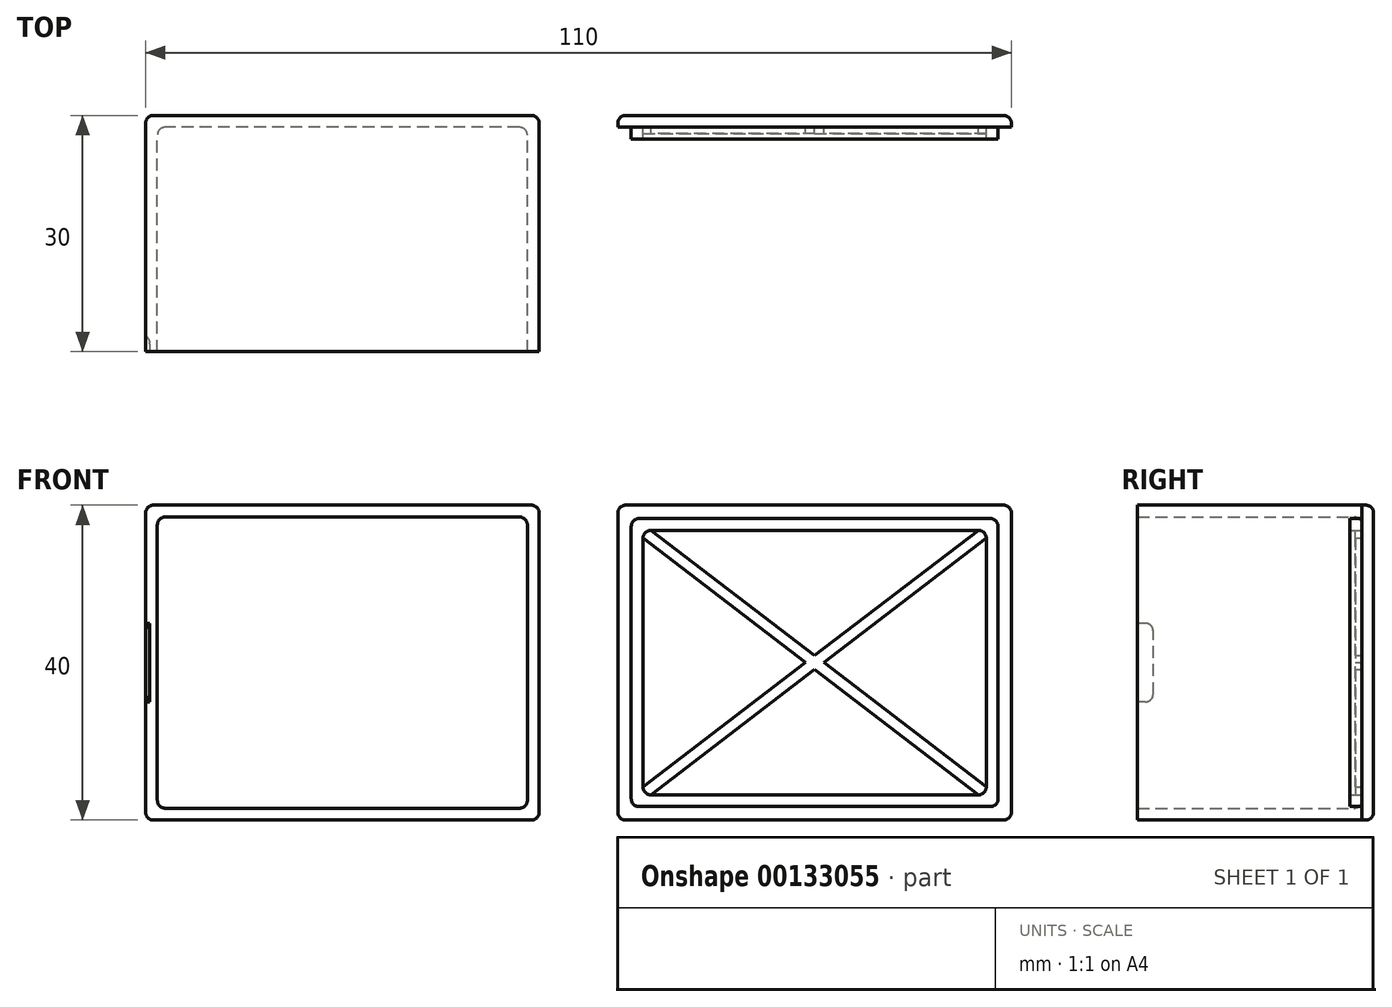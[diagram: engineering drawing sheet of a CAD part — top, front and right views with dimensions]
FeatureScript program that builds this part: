
annotation { "Feature Type Name" : "Feature", "Feature Type Description" : "" }
export const myFeature = defineFeature(function(context is Context, id is Id, definition is map)
    precondition{}
    {
        {
            var Q0;
            Q0=qCreatedBy(makeId("Front.planeOp"),FACE);
            var sketch = newSketch(context, id + "F0", { "sketchPlane" : qUnion([Q0])});
            skLineSegment(sketch, "E0.bottom", {"start": v(0, 0) * mm, "end": v(50, 0) * mm});
            skLineSegment(sketch, "E0.top", {"start": v(0, 40) * mm, "end": v(50, 40) * mm});
            skLineSegment(sketch, "E0.left", {"start": v(0, 0) * mm, "end": v(0, 40) * mm});
            skLineSegment(sketch, "E0.right", {"start": v(50, 0) * mm, "end": v(50, 40) * mm});
            skLineSegment(sketch, "E1.bottom", {"start": v(1.5, 38.5) * mm, "end": v(48.5, 38.5) * mm});
            skLineSegment(sketch, "E1.top", {"start": v(1.5, 1.5) * mm, "end": v(48.5, 1.5) * mm});
            skLineSegment(sketch, "E1.left", {"start": v(1.5, 38.5) * mm, "end": v(1.5, 1.5) * mm});
            skLineSegment(sketch, "E1.right", {"start": v(48.5, 38.5) * mm, "end": v(48.5, 1.5) * mm});
            skLineSegment(sketch, "E2", {"start": v(25, 0) * mm, "end": v(25, 40) * mm, "construction": true});
            skLineSegment(sketch, "E3", {"start": v(0, 20) * mm, "end": v(50, 20) * mm, "construction": true});
            skLineSegment(sketch, "E4", {"start": v(60, 20) * mm, "end": v(110, 20) * mm, "construction": true});
            skLineSegment(sketch, "E5", {"start": v(85, 0) * mm, "end": v(85, 40) * mm, "construction": true});
            skLineSegment(sketch, "E6.bottom", {"start": v(60, 40) * mm, "end": v(110, 40) * mm});
            skLineSegment(sketch, "E6.top", {"start": v(60, 0) * mm, "end": v(110, 0) * mm});
            skLineSegment(sketch, "E6.left", {"start": v(60, 40) * mm, "end": v(60, 0) * mm});
            skLineSegment(sketch, "E6.right", {"start": v(110, 40) * mm, "end": v(110, 0) * mm});
            skLineSegment(sketch, "E7.bottom", {"start": v(61.5, 38.5) * mm, "end": v(108.5, 38.5) * mm, "construction": true});
            skLineSegment(sketch, "E7.top", {"start": v(61.5, 1.5) * mm, "end": v(108.5, 1.5) * mm, "construction": true});
            skLineSegment(sketch, "E7.left", {"start": v(61.5, 38.5) * mm, "end": v(61.5, 1.5) * mm, "construction": true});
            skLineSegment(sketch, "E7.right", {"start": v(108.5, 38.5) * mm, "end": v(108.5, 1.5) * mm, "construction": true});
            skLineSegment(sketch, "E8.bottom", {"start": v(61.7, 38.3) * mm, "end": v(108.3, 38.3) * mm});
            skLineSegment(sketch, "E8.top", {"start": v(61.7, 1.7) * mm, "end": v(108.3, 1.7) * mm});
            skLineSegment(sketch, "E8.left", {"start": v(61.7, 38.3) * mm, "end": v(61.7, 1.7) * mm});
            skLineSegment(sketch, "E8.right", {"start": v(108.3, 38.3) * mm, "end": v(108.3, 1.7) * mm});
            skLineSegment(sketch, "E9", {"start": v(1.5, 38.5) * mm, "end": v(0, 38.5) * mm, "construction": true});
            skLineSegment(sketch, "E10", {"start": v(1.5, 38.5) * mm, "end": v(1.5, 40) * mm, "construction": true});
            skText(sketch, "E11", { "text": "Длина\nШирина\nТолщина стенок\nЗазор в ответной части", "fontName": "OpenSans-Regular.ttf"});
            skLineSegment(sketch, "E12", {"start": v(12.68, 60) * mm, "end": v(49.68, 60) * mm, "construction": true});
            skLineSegment(sketch, "E13", {"start": v(12.68, 57.5) * mm, "end": v(59.68, 57.5) * mm, "construction": true});
            skLineSegment(sketch, "E14", {"start": v(12.68, 55) * mm, "end": v(14.18, 55) * mm, "construction": true});
            skLineSegment(sketch, "E15", {"start": v(12.68, 52.5) * mm, "end": v(12.88, 52.5) * mm, "construction": true});
            skLineSegment(sketch, "E16", {"start": v(61.5, 38.5) * mm, "end": v(61.5, 40) * mm, "construction": true});
            skLineSegment(sketch, "E17", {"start": v(61.5, 38.5) * mm, "end": v(60, 38.5) * mm, "construction": true});
            skLineSegment(sketch, "E18", {"start": v(61.7, 38.3) * mm, "end": v(61.7, 38.5) * mm, "construction": true});
            skLineSegment(sketch, "E19", {"start": v(61.7, 38.3) * mm, "end": v(61.5, 38.3) * mm, "construction": true});
            skLineSegment(sketch, "E20.bottom", {"start": v(63.2, 36.8) * mm, "end": v(106.8, 36.8) * mm});
            skLineSegment(sketch, "E20.top", {"start": v(63.2, 3.2) * mm, "end": v(106.8, 3.2) * mm});
            skLineSegment(sketch, "E20.left", {"start": v(63.2, 36.8) * mm, "end": v(63.2, 3.2) * mm});
            skLineSegment(sketch, "E20.right", {"start": v(106.8, 36.8) * mm, "end": v(106.8, 3.2) * mm});
            skLineSegment(sketch, "E21", {"start": v(63.2, 36.8) * mm, "end": v(63.2, 38.3) * mm, "construction": true});
            skLineSegment(sketch, "E22", {"start": v(63.2, 36.8) * mm, "end": v(61.7, 36.8) * mm, "construction": true});
            const initialGuessF0  = {"E11": [-0.0124, 0.05874, 1, 0, 0.00126]};
            skSetInitialGuess(sketch, initialGuessF0);
            skSolve(sketch);
        }
        {
            var Q0;
            Q0=makeQuery(id+"F0.imprint","IMPRINT",FACE,{"disambiguationData":[TD([[makeQuery(id+"F0.imprint","IMPRINT",EDGE,{"derivedFrom":sQuery(id+"F0.wireOp",EDGE,"E1.bottom")}),-1.0]])]});
            var Q1;
            Q1=makeQuery(id+"F0.imprint","IMPRINT",FACE,{"disambiguationData":[TD([[makeQuery(id+"F0.imprint","IMPRINT",EDGE,{"derivedFrom":sQuery(id+"F0.wireOp",EDGE,"E0.bottom")}),1.0]])]});
            var Q2;
            Q2=makeQuery(id+"F0.imprint","IMPRINT",FACE,{"disambiguationData":[TD([[makeQuery(id+"F0.imprint","IMPRINT",EDGE,{"derivedFrom":sQuery(id+"F0.wireOp",EDGE,"E6.bottom")}),-1.0]])]});
            var Q3;
            Q3=makeQuery(id+"F0.imprint","IMPRINT",FACE,{"disambiguationData":[TD([[makeQuery(id+"F0.imprint","IMPRINT",EDGE,{"derivedFrom":sQuery(id+"F0.wireOp",EDGE,"E7.bottom")}),-1.0]])]});
            var Q4;
            Q4=makeQuery(id+"F0.imprint","IMPRINT",FACE,{"disambiguationData":[TD([[makeQuery(id+"F0.imprint","IMPRINT",EDGE,{"derivedFrom":sQuery(id+"F0.wireOp",EDGE,"E8.bottom")}),-1.0]])]});
            var Q5;
            Q5=makeQuery(id+"F0.imprint","IMPRINT",FACE,{"disambiguationData":[TD([[makeQuery(id+"F0.imprint","IMPRINT",EDGE,{"derivedFrom":sQuery(id+"F0.wireOp",EDGE,"E20.bottom")}),-1.0]])]});
            extrude(context, id + "F1", {"entities" : qUnion([Q0, Q1, Q2, Q3, Q4, Q5]), "depth" : 1.5 * mm, "offsetDistance" : 25 * mm});
        }
        {
            var Q0;
            Q0=makeQuery(id+"F0.imprint","IMPRINT",FACE,{"disambiguationData":[TD([[makeQuery(id+"F0.imprint","IMPRINT",EDGE,{"derivedFrom":sQuery(id+"F0.wireOp",EDGE,"E0.bottom")}),1.0]])]});
            extrude(context, id + "F2", {"entities" : qUnion([Q0]), "operationType" : NewBodyOperationType.ADD, "depth" : 30 * mm, "offsetDistance" : 25 * mm});
        }
        {
            var Q0;
            Q0=makeQuery(id+"F0.imprint","IMPRINT",FACE,{"disambiguationData":[TD([[makeQuery(id+"F0.imprint","IMPRINT",EDGE,{"derivedFrom":sQuery(id+"F0.wireOp",EDGE,"E8.bottom")}),-1.0]])]});
            extrude(context, id + "F3", {"entities" : qUnion([Q0]), "operationType" : NewBodyOperationType.ADD, "depth" : (1 + 2) * mm});
        }
        {
            var Q0;
            {var subQ0=sQuery(id+"F0.wireOp",EDGE,"E0.right");var subQ1=sQuery(id+"F0.wireOp",EDGE,"E0.bottom");Q0=makeQuery(id+"F2.boolean.opBoolean","MERGE",EDGE,{"derivedFrom":[makeQuery(id+"F1.opExtrude","SWEPT_EDGE",EDGE,{"disambiguationData":[OSD([subQ1,subQ0])]}),makeQuery(id+"F2.opExtrude","SWEPT_EDGE",EDGE,{"disambiguationData":[OSD([subQ1,subQ0])]})]});}
            var Q1;
            {var subQ0=sQuery(id+"F0.wireOp",EDGE,"E0.left");var subQ1=sQuery(id+"F0.wireOp",EDGE,"E0.bottom");Q1=makeQuery(id+"F2.boolean.opBoolean","MERGE",EDGE,{"derivedFrom":[makeQuery(id+"F1.opExtrude","SWEPT_EDGE",EDGE,{"disambiguationData":[OSD([subQ1,subQ0])]}),makeQuery(id+"F2.opExtrude","SWEPT_EDGE",EDGE,{"disambiguationData":[OSD([subQ1,subQ0])]})]});}
            var Q2;
            {var subQ0=sQuery(id+"F0.wireOp",EDGE,"E0.left");var subQ1=sQuery(id+"F0.wireOp",EDGE,"E0.top");Q2=makeQuery(id+"F2.boolean.opBoolean","MERGE",EDGE,{"derivedFrom":[makeQuery(id+"F1.opExtrude","SWEPT_EDGE",EDGE,{"disambiguationData":[OSD([subQ1,subQ0])]}),makeQuery(id+"F2.opExtrude","SWEPT_EDGE",EDGE,{"disambiguationData":[OSD([subQ1,subQ0])]})]});}
            var Q3;
            {var subQ0=sQuery(id+"F0.wireOp",EDGE,"E0.right");var subQ1=sQuery(id+"F0.wireOp",EDGE,"E0.top");Q3=makeQuery(id+"F2.boolean.opBoolean","MERGE",EDGE,{"derivedFrom":[makeQuery(id+"F1.opExtrude","SWEPT_EDGE",EDGE,{"disambiguationData":[OSD([subQ1,subQ0])]}),makeQuery(id+"F2.opExtrude","SWEPT_EDGE",EDGE,{"disambiguationData":[OSD([subQ1,subQ0])]})]});}
            var Q4;
            Q4=makeQuery(id+"F1.opExtrude","CAP_EDGE",EDGE,{"disambiguationData":[OSD([sQuery(id+"F0.wireOp",EDGE,"E0.top")])],"isStart":true});
            var Q5;
            Q5=makeQuery(id+"F1.opExtrude","CAP_EDGE",EDGE,{"disambiguationData":[OSD([sQuery(id+"F0.wireOp",EDGE,"E0.left")])],"isStart":true});
            var Q6;
            Q6=makeQuery(id+"F1.opExtrude","CAP_EDGE",EDGE,{"disambiguationData":[OSD([sQuery(id+"F0.wireOp",EDGE,"E0.bottom")])],"isStart":true});
            var Q7;
            Q7=makeQuery(id+"F1.opExtrude","CAP_EDGE",EDGE,{"disambiguationData":[OSD([sQuery(id+"F0.wireOp",EDGE,"E0.right")])],"isStart":true});
            var Q8;
            Q8=makeQuery(id+"F1.opExtrude","CAP_EDGE",EDGE,{"disambiguationData":[OSD([sQuery(id+"F0.wireOp",EDGE,"E6.bottom")])],"isStart":true});
            var Q9;
            Q9=makeQuery(id+"F1.opExtrude","CAP_EDGE",EDGE,{"disambiguationData":[OSD([sQuery(id+"F0.wireOp",EDGE,"E6.left")])],"isStart":true});
            var Q10;
            Q10=makeQuery(id+"F1.opExtrude","CAP_EDGE",EDGE,{"disambiguationData":[OSD([sQuery(id+"F0.wireOp",EDGE,"E6.top")])],"isStart":true});
            var Q11;
            Q11=makeQuery(id+"F1.opExtrude","CAP_EDGE",EDGE,{"disambiguationData":[OSD([sQuery(id+"F0.wireOp",EDGE,"E6.right")])],"isStart":true});
            var Q12;
            Q12=makeQuery(id+"F1.opExtrude","SWEPT_EDGE",EDGE,{"disambiguationData":[OSD([sQuery(id+"F0.wireOp",EDGE,"E6.top"),sQuery(id+"F0.wireOp",EDGE,"E6.left")])]});
            var Q13;
            Q13=makeQuery(id+"F1.opExtrude","SWEPT_EDGE",EDGE,{"disambiguationData":[OSD([sQuery(id+"F0.wireOp",EDGE,"E6.bottom"),sQuery(id+"F0.wireOp",EDGE,"E6.left")])]});
            var Q14;
            Q14=makeQuery(id+"F1.opExtrude","SWEPT_EDGE",EDGE,{"disambiguationData":[OSD([sQuery(id+"F0.wireOp",EDGE,"E6.bottom"),sQuery(id+"F0.wireOp",EDGE,"E6.right")])]});
            var Q15;
            Q15=makeQuery(id+"F1.opExtrude","SWEPT_EDGE",EDGE,{"disambiguationData":[OSD([sQuery(id+"F0.wireOp",EDGE,"E6.top"),sQuery(id+"F0.wireOp",EDGE,"E6.right")])]});
            var Q16;
            Q16=makeQuery(id+"F2.opExtrude","SWEPT_EDGE",EDGE,{"disambiguationData":[OSD([sQuery(id+"F0.wireOp",EDGE,"E1.bottom"),sQuery(id+"F0.wireOp",EDGE,"E1.right")])]});
            var Q17;
            Q17=makeQuery(id+"F2.opExtrude","SWEPT_EDGE",EDGE,{"disambiguationData":[OSD([sQuery(id+"F0.wireOp",EDGE,"E1.top"),sQuery(id+"F0.wireOp",EDGE,"E1.right")])]});
            var Q18;
            Q18=makeQuery(id+"F2.opExtrude","SWEPT_EDGE",EDGE,{"disambiguationData":[OSD([sQuery(id+"F0.wireOp",EDGE,"E1.bottom"),sQuery(id+"F0.wireOp",EDGE,"E1.left")])]});
            var Q19;
            Q19=makeQuery(id+"F2.opExtrude","SWEPT_EDGE",EDGE,{"disambiguationData":[OSD([sQuery(id+"F0.wireOp",EDGE,"E1.top"),sQuery(id+"F0.wireOp",EDGE,"E1.left")])]});
            var Q20;
            Q20=makeQuery(id+"F2.boolean.opBoolean","INTERSECT",EDGE,{"derivedFrom":[makeQuery(id+"F1.opExtrude","CAP_FACE",FACE,{"disambiguationData":[OSD([sQuery(id+"F0.wireOp",EDGE,"E0.bottom"),sQuery(id+"F0.wireOp",EDGE,"E0.top"),sQuery(id+"F0.wireOp",EDGE,"E0.left"),sQuery(id+"F0.wireOp",EDGE,"E0.right")])],"isStart":false}),makeQuery(id+"F2.opExtrude","SWEPT_FACE",FACE,{"disambiguationData":[OSD([sQuery(id+"F0.wireOp",EDGE,"E1.left")])]})]});
            var Q21;
            Q21=makeQuery(id+"F2.boolean.opBoolean","INTERSECT",EDGE,{"derivedFrom":[makeQuery(id+"F1.opExtrude","CAP_FACE",FACE,{"disambiguationData":[OSD([sQuery(id+"F0.wireOp",EDGE,"E0.bottom"),sQuery(id+"F0.wireOp",EDGE,"E0.top"),sQuery(id+"F0.wireOp",EDGE,"E0.left"),sQuery(id+"F0.wireOp",EDGE,"E0.right")])],"isStart":false}),makeQuery(id+"F2.opExtrude","SWEPT_FACE",FACE,{"disambiguationData":[OSD([sQuery(id+"F0.wireOp",EDGE,"E1.bottom")])]})]});
            var Q22;
            Q22=makeQuery(id+"F2.boolean.opBoolean","INTERSECT",EDGE,{"derivedFrom":[makeQuery(id+"F1.opExtrude","CAP_FACE",FACE,{"disambiguationData":[OSD([sQuery(id+"F0.wireOp",EDGE,"E0.bottom"),sQuery(id+"F0.wireOp",EDGE,"E0.top"),sQuery(id+"F0.wireOp",EDGE,"E0.left"),sQuery(id+"F0.wireOp",EDGE,"E0.right")])],"isStart":false}),makeQuery(id+"F2.opExtrude","SWEPT_FACE",FACE,{"disambiguationData":[OSD([sQuery(id+"F0.wireOp",EDGE,"E1.right")])]})]});
            var Q23;
            Q23=makeQuery(id+"F2.boolean.opBoolean","INTERSECT",EDGE,{"derivedFrom":[makeQuery(id+"F1.opExtrude","CAP_FACE",FACE,{"disambiguationData":[OSD([sQuery(id+"F0.wireOp",EDGE,"E0.bottom"),sQuery(id+"F0.wireOp",EDGE,"E0.top"),sQuery(id+"F0.wireOp",EDGE,"E0.left"),sQuery(id+"F0.wireOp",EDGE,"E0.right")])],"isStart":false}),makeQuery(id+"F2.opExtrude","SWEPT_FACE",FACE,{"disambiguationData":[OSD([sQuery(id+"F0.wireOp",EDGE,"E1.top")])]})]});
            var Q24;
            Q24=makeQuery(id+"F3.opExtrude","SWEPT_EDGE",EDGE,{"disambiguationData":[OSD([sQuery(id+"F0.wireOp",EDGE,"E8.top"),sQuery(id+"F0.wireOp",EDGE,"E8.left")])]});
            var Q25;
            Q25=makeQuery(id+"F3.opExtrude","SWEPT_EDGE",EDGE,{"disambiguationData":[OSD([sQuery(id+"F0.wireOp",EDGE,"E8.top"),sQuery(id+"F0.wireOp",EDGE,"E8.right")])]});
            var Q26;
            Q26=makeQuery(id+"F3.opExtrude","SWEPT_EDGE",EDGE,{"disambiguationData":[OSD([sQuery(id+"F0.wireOp",EDGE,"E8.bottom"),sQuery(id+"F0.wireOp",EDGE,"E8.right")])]});
            var Q27;
            Q27=makeQuery(id+"F3.opExtrude","SWEPT_EDGE",EDGE,{"disambiguationData":[OSD([sQuery(id+"F0.wireOp",EDGE,"E8.bottom"),sQuery(id+"F0.wireOp",EDGE,"E8.left")])]});
            var Q28;
            Q28=makeQuery(id+"F3.opExtrude","SWEPT_EDGE",EDGE,{"disambiguationData":[OSD([sQuery(id+"F0.wireOp",EDGE,"E20.bottom"),sQuery(id+"F0.wireOp",EDGE,"E20.left")])]});
            var Q29;
            Q29=makeQuery(id+"F3.opExtrude","SWEPT_EDGE",EDGE,{"disambiguationData":[OSD([sQuery(id+"F0.wireOp",EDGE,"E20.bottom"),sQuery(id+"F0.wireOp",EDGE,"E20.right")])]});
            var Q30;
            Q30=makeQuery(id+"F3.opExtrude","SWEPT_EDGE",EDGE,{"disambiguationData":[OSD([sQuery(id+"F0.wireOp",EDGE,"E20.top"),sQuery(id+"F0.wireOp",EDGE,"E20.right")])]});
            var Q31;
            Q31=makeQuery(id+"F3.opExtrude","SWEPT_EDGE",EDGE,{"disambiguationData":[OSD([sQuery(id+"F0.wireOp",EDGE,"E20.top"),sQuery(id+"F0.wireOp",EDGE,"E20.left")])]});
            fillet(context, id + "F4", {"entities" : qUnion([Q0, Q1, Q2, Q3, Q4, Q5, Q6, Q7, Q8, Q9, Q10, Q11, Q12, Q13, Q14, Q15, Q16, Q17, Q18, Q19, Q20, Q21, Q22, Q23, Q24, Q25, Q26, Q27, Q28, Q29, Q30, Q31]), "radius" : 1 * mm, "tangentPropagation" : true, "allowEdgeOverflow" : false});
        }
        {
            var Q0;
            Q0=makeQuery(id+"F3.boolean.opBoolean","SPLIT",FACE,{"disambiguationData":[TD([makeQuery(id+"F3.opExtrude","SWEPT_FACE",FACE,{"disambiguationData":[OSD([sQuery(id+"F0.wireOp",EDGE,"E20.bottom")])]})])],"derivedFrom":makeQuery(id+"F1.opExtrude","CAP_FACE",FACE,{"disambiguationData":[OSD([sQuery(id+"F0.wireOp",EDGE,"E6.bottom"),sQuery(id+"F0.wireOp",EDGE,"E6.top"),sQuery(id+"F0.wireOp",EDGE,"E6.left"),sQuery(id+"F0.wireOp",EDGE,"E6.right")])],"isStart":false})});
            var sketch = newSketch(context, id + "F5", { "sketchPlane" : qUnion([Q0])});
            skLineSegment(sketch, "E23", {"start": v(63.2, 4.2) * mm, "end": v(105.8, 36.8) * mm});
            skLineSegment(sketch, "E24", {"start": v(106.8, 35.8) * mm, "end": v(64.2, 3.2) * mm});
            skLineSegment(sketch, "E25", {"start": v(63.2, 35.8) * mm, "end": v(105.8, 3.2) * mm});
            skLineSegment(sketch, "E26", {"start": v(106.8, 4.2) * mm, "end": v(64.2, 36.8) * mm});
            skSolve(sketch);
        }
        {
            var Q0;
            Q0 = qSketchRegion(id + "F5", true);
            var Q1;
            {var subQ0=sQuery(id+"F5.wireOp",EDGE,"E25");var subQ1=sQuery(id+"F5.wireOp",EDGE,"E23");var subQ2=makeQuery(id+"F5.imprint","INTERSECT",VERTEX,{"derivedFrom":[subQ1,subQ0]});Q1=makeQuery(id+"F5.imprint","IMPRINT",FACE,{"disambiguationData":[TD([[makeQuery(id+"F5.imprint","IMPRINT",EDGE,{"disambiguationData":[TD([[subQ2,-1.0]])],"derivedFrom":subQ1}),1.0]])]});}
            var Q2;
            {var subQ0=sQuery(id+"F5.wireOp",EDGE,"E23");var subQ7=sQuery(id+"F5.wireOp",EDGE,"E25");var subQ8=makeQuery(id+"F5.imprint","INTERSECT",VERTEX,{"derivedFrom":[subQ0,subQ7]});Q2=makeQuery(id+"F5.imprint","IMPRINT",FACE,{"disambiguationData":[TD([[makeQuery(id+"F5.imprint","IMPRINT",EDGE,{"disambiguationData":[TD([[subQ8,-1.0]])],"derivedFrom":subQ7}),-1.0]])]});}
            var Q3;
            {var subQ0=sQuery(id+"F5.wireOp",EDGE,"E23");var subQ7=sQuery(id+"F5.wireOp",EDGE,"E26");var subQ8=makeQuery(id+"F5.imprint","INTERSECT",VERTEX,{"derivedFrom":[subQ0,subQ7]});Q3=makeQuery(id+"F5.imprint","IMPRINT",FACE,{"disambiguationData":[TD([[makeQuery(id+"F5.imprint","IMPRINT",EDGE,{"disambiguationData":[TD([[subQ8,1.0]])],"derivedFrom":subQ7}),-1.0]])]});}
            var Q4;
            {var subQ0=sQuery(id+"F5.wireOp",EDGE,"E26");var subQ1=sQuery(id+"F5.wireOp",EDGE,"E24");var subQ2=makeQuery(id+"F5.imprint","INTERSECT",VERTEX,{"derivedFrom":[subQ1,subQ0]});Q4=makeQuery(id+"F5.imprint","IMPRINT",FACE,{"disambiguationData":[TD([[makeQuery(id+"F5.imprint","IMPRINT",EDGE,{"disambiguationData":[TD([[subQ2,-1.0]])],"derivedFrom":subQ1}),1.0]])]});}
            extrude(context, id + "F6", {"entities" : qUnion([Q0, Q1, Q2, Q3, Q4]), "operationType" : NewBodyOperationType.ADD, "depth" : 0.8 * mm, "offsetDistance" : 25 * mm});
        }
        {
            var Q0;
            Q0=makeQuery(id+"F2.opExtrude","CAP_FACE",FACE,{"disambiguationData":[OSD([sQuery(id+"F0.wireOp",EDGE,"E0.bottom"),sQuery(id+"F0.wireOp",EDGE,"E0.top"),sQuery(id+"F0.wireOp",EDGE,"E0.left"),sQuery(id+"F0.wireOp",EDGE,"E0.right"),sQuery(id+"F0.wireOp",EDGE,"E1.bottom"),sQuery(id+"F0.wireOp",EDGE,"E1.top"),sQuery(id+"F0.wireOp",EDGE,"E1.left"),sQuery(id+"F0.wireOp",EDGE,"E1.right")])],"isStart":false});
            var sketch = newSketch(context, id + "F7", { "sketchPlane" : qUnion([Q0])});
            skLineSegment(sketch, "E27.bottom", {"start": v(0, 15) * mm, "end": v(0.5, 15) * mm});
            skLineSegment(sketch, "E27.top", {"start": v(0, 25) * mm, "end": v(0.5, 25) * mm});
            skLineSegment(sketch, "E27.left", {"start": v(0, 25) * mm, "end": v(0, 15) * mm});
            skLineSegment(sketch, "E27.right", {"start": v(0.5, 25) * mm, "end": v(0.5, 15) * mm});
            skPoint(sketch, "E28", {"position": v(0.5, 20) * mm});
            skPoint(sketch, "E29", {"position": v(0, 20) * mm});
            skSolve(sketch);
        }
        {
            var Q0;
            Q0=makeQuery(id+"F7.imprint","IMPRINT",FACE,{"disambiguationData":[TD([[makeQuery(id+"F7.imprint","IMPRINT",EDGE,{"derivedFrom":sQuery(id+"F7.wireOp",EDGE,"E27.bottom")}),1.0]])]});
            extrude(context, id + "F8", {"entities" : qUnion([Q0]), "operationType" : NewBodyOperationType.REMOVE, "oppositeDirection" : true, "depth" : 2 * mm, "offsetDistance" : 25 * mm});
        }
        {
            var Q0;
            Q0=makeQuery(id+"F8.boolean.opBoolean","COPY",EDGE,{"derivedFrom":makeQuery(id+"F8.opExtrude","CAP_EDGE",EDGE,{"disambiguationData":[OSD([sQuery(id+"F7.wireOp",EDGE,"E27.bottom")])],"isStart":false})});
            var Q1;
            Q1=makeQuery(id+"F8.boolean.opBoolean","COPY",EDGE,{"derivedFrom":makeQuery(id+"F8.opExtrude","CAP_EDGE",EDGE,{"disambiguationData":[OSD([sQuery(id+"F7.wireOp",EDGE,"E27.top")])],"isStart":false})});
            var Q2;
            Q2=makeQuery(id+"F8.boolean.opBoolean","COPY",EDGE,{"derivedFrom":makeQuery(id+"F8.opExtrude","CAP_EDGE",EDGE,{"disambiguationData":[OSD([sQuery(id+"F7.wireOp",EDGE,"E27.right")])],"isStart":false})});
            fillet(context, id + "F9", {"entities" : qUnion([Q0, Q1, Q2]), "radius" : 1 * mm, "tangentPropagation" : true, "allowEdgeOverflow" : false});
        }
    });
